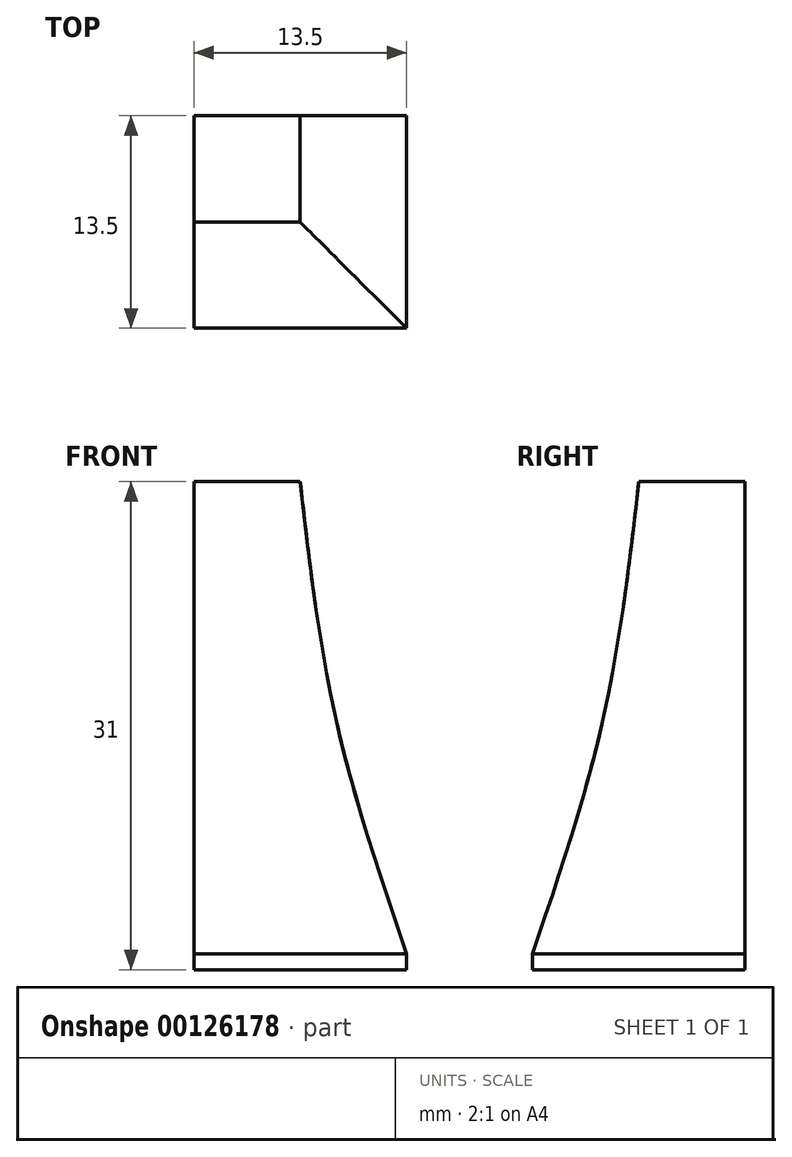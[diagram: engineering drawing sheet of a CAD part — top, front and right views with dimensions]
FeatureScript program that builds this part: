
annotation { "Feature Type Name" : "Feature", "Feature Type Description" : "" }
export const myFeature = defineFeature(function(context is Context, id is Id, definition is map)
    precondition{}
    {
        {
            var Q0;
            Q0=qCreatedBy(makeId("Top.planeOp"),FACE);
            var sketch = newSketch(context, id + "F0", { "sketchPlane" : qUnion([Q0])});
            skLineSegment(sketch, "E0.bottom", {"start": v(0, 0) * mm, "end": v(-13.5, 0) * mm});
            skLineSegment(sketch, "E0.top", {"start": v(0, 13.5) * mm, "end": v(-13.5, 13.5) * mm});
            skLineSegment(sketch, "E0.left", {"start": v(0, 0) * mm, "end": v(0, 13.5) * mm});
            skLineSegment(sketch, "E0.right", {"start": v(-13.5, 0) * mm, "end": v(-13.5, 13.5) * mm});
            skSolve(sketch);
        }
        {
            var Q0;
            Q0 = qSketchRegion(id + "F0", true);
            extrude(context, id + "F1", {"entities" : qUnion([Q0]), "depth" : 30 * mm});
        }
        {
            var Q0;
            Q0=makeQuery(id+"F1.opExtrude","SWEPT_FACE",FACE,{"disambiguationData":[OSD([sQuery(id+"F0.wireOp",EDGE,"E0.bottom")])]});
            var sketch = newSketch(context, id + "F2", { "sketchPlane" : qUnion([Q0])});
            skLineSegment(sketch, "E1", {"start": v(-13.5, 15) * mm, "end": v(0, 15) * mm, "construction": true});
            skPoint(sketch, "E2", {"position": v(-4.5, 15) * mm});
            skLineSegment(sketch, "E3", {"start": v(0, 0) * mm, "end": v(0, 30) * mm});
            skPoint(sketch, "E4", {"position": v(-6.75, 30) * mm});
            skLineSegment(sketch, "E5", {"start": v(-6.75, 30) * mm, "end": v(0, 30) * mm});
            skFitSpline(sketch, "E6", {"points": [v(-6.75, 30) * mm, v(-4.5, 15) * mm, v(0, 0) * mm], "startDerivative": vector(3.45, -30.36) * mm, "endDerivative": vector(10.04, -29.64) * mm});
            skSolve(sketch);
        }
        {
            var Q0;
            Q0 = qSketchRegion(id + "F2", true);
            extrude(context, id + "F3", {"entities" : qUnion([Q0]), "operationType" : NewBodyOperationType.REMOVE, "oppositeDirection" : true, "depth" : 13.5 * mm});
        }
        {
            var Q0;
            Q0=makeQuery(id+"F1.opExtrude","SWEPT_FACE",FACE,{"disambiguationData":[OSD([sQuery(id+"F0.wireOp",EDGE,"E0.right")])]});
            var sketch = newSketch(context, id + "F4", { "sketchPlane" : qUnion([Q0])});
            skLineSegment(sketch, "E7", {"start": v(-13.5, 15) * mm, "end": v(0, 15) * mm, "construction": true});
            skPoint(sketch, "E8", {"position": v(-4.5, 15) * mm});
            skLineSegment(sketch, "E9", {"start": v(0, 30) * mm, "end": v(0, 0) * mm});
            skPoint(sketch, "E10", {"position": v(-6.75, 30) * mm});
            skFitSpline(sketch, "E11", {"points": [v(-6.75, 30) * mm, v(-4.5, 15) * mm, v(0, 0) * mm], "startDerivative": vector(3.45, -30.36) * mm, "endDerivative": vector(10.04, -29.64) * mm});
            skLineSegment(sketch, "E12", {"start": v(-6.75, 30) * mm, "end": v(0, 30) * mm});
            skSolve(sketch);
        }
        {
            var Q0;
            Q0=makeQuery(id+"F4.imprint","IMPRINT",FACE,{"disambiguationData":[TD([[makeQuery(id+"F4.imprint","IMPRINT",EDGE,{"derivedFrom":sQuery(id+"F4.wireOp",EDGE,"ece0fcbd-eaa2-4a0e-a779-fdd9259d91b3")}),-1.0]])]});
            var Q1;
            Q1=makeQuery(id+"F4.imprint","IMPRINT",FACE,{"disambiguationData":[TD([[makeQuery(id+"F4.imprint","IMPRINT",EDGE,{"derivedFrom":sQuery(id+"F4.wireOp",EDGE,"E9")}),-1.0]])]});
            extrude(context, id + "F5", {"entities" : qUnion([Q0, Q1]), "operationType" : NewBodyOperationType.REMOVE, "oppositeDirection" : true, "depth" : 13.5 * mm});
        }
        {
            var Q0;
            Q0=makeQuery(id+"F1.opExtrude","CAP_FACE",FACE,{"disambiguationData":[OSD([sQuery(id+"F0.wireOp",EDGE,"E0.bottom"),sQuery(id+"F0.wireOp",EDGE,"E0.top"),sQuery(id+"F0.wireOp",EDGE,"E0.left"),sQuery(id+"F0.wireOp",EDGE,"E0.right")])],"isStart":true});
            var sketch = newSketch(context, id + "F6", { "sketchPlane" : qUnion([Q0])});
            skLineSegment(sketch, "E13.bottom", {"start": v(0, 0) * mm, "end": v(-13.5, 0) * mm});
            skLineSegment(sketch, "E13.top", {"start": v(0, -13.5) * mm, "end": v(-13.5, -13.5) * mm});
            skLineSegment(sketch, "E13.left", {"start": v(0, 0) * mm, "end": v(0, -13.5) * mm});
            skLineSegment(sketch, "E13.right", {"start": v(-13.5, 0) * mm, "end": v(-13.5, -13.5) * mm});
            skSolve(sketch);
        }
        {
            var Q0;
            Q0 = qSketchRegion(id + "F6", true);
            extrude(context, id + "F7", {"entities" : qUnion([Q0]), "operationType" : NewBodyOperationType.ADD, "depth" : 1 * mm});
        }
    });
